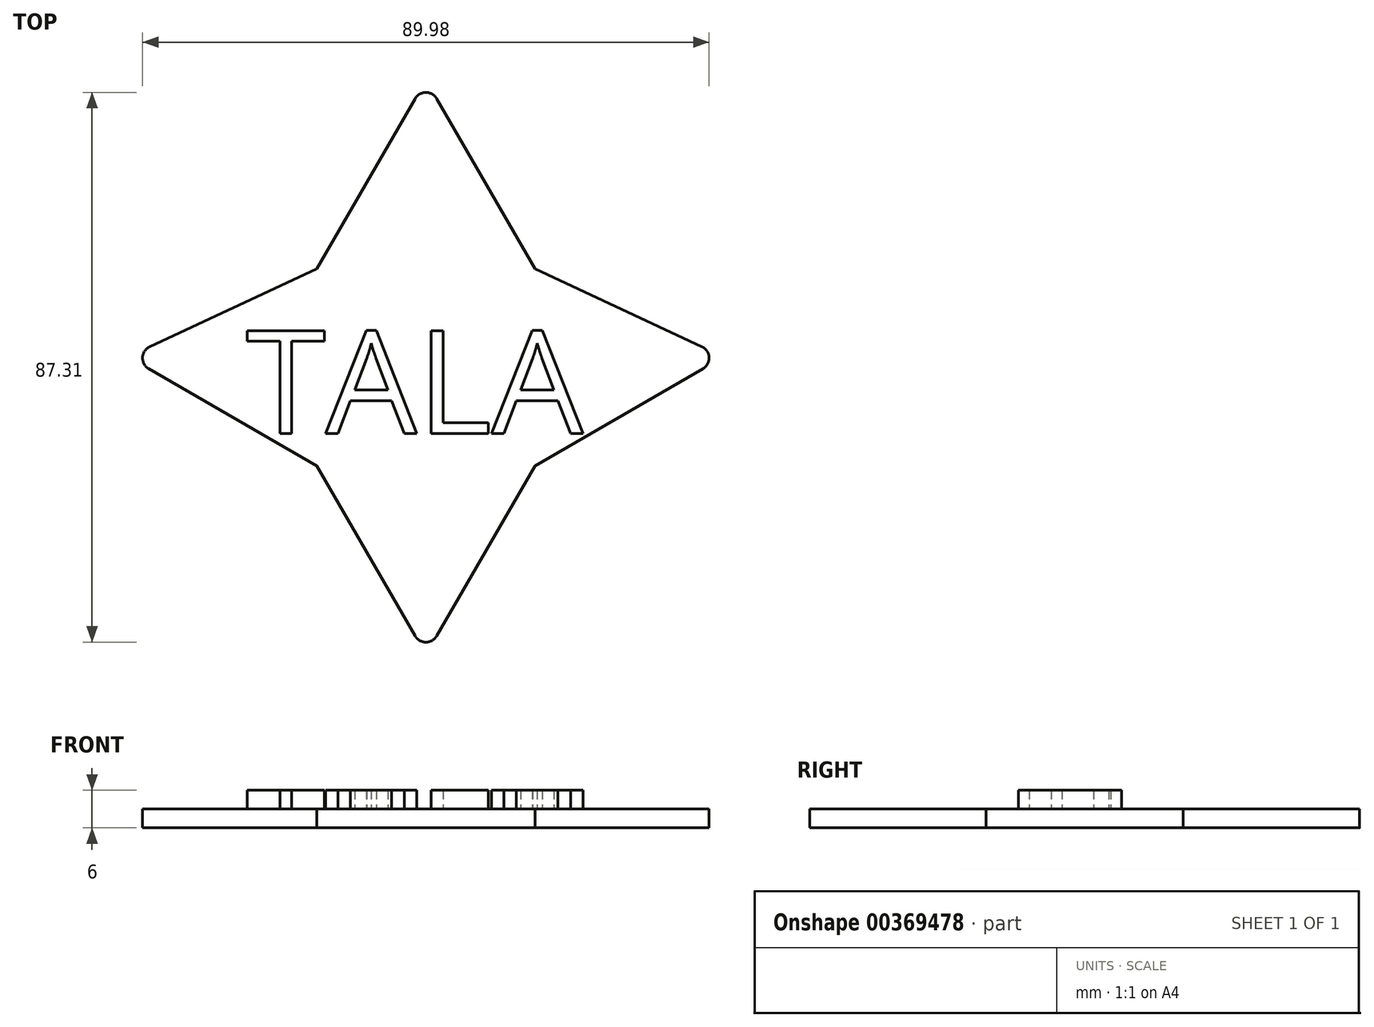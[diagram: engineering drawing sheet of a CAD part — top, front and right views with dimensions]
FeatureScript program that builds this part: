
annotation { "Feature Type Name" : "Feature", "Feature Type Description" : "" }
export const myFeature = defineFeature(function(context is Context, id is Id, definition is map)
    precondition{}
    {
        {
            var Q0;
            Q0=qCreatedBy(makeId("Top.planeOp"),FACE);
            var sketch = newSketch(context, id + "F0", { "sketchPlane" : qUnion([Q0])});
            skLineSegment(sketch, "E0", {"start": v(0, 0) * mm, "end": v(15.59, 27) * mm});
            skLineSegment(sketch, "E1", {"start": v(19.05, 27) * mm, "end": v(34.64, 0) * mm});
            skLineSegment(sketch, "E2", {"start": v(0, 0) * mm, "end": v(-26.52, -12.37) * mm});
            skLineSegment(sketch, "E3", {"start": v(-26.67, -15.91) * mm, "end": v(0, -31.3) * mm});
            skLineSegment(sketch, "E4", {"start": v(17.32, 30) * mm, "end": v(17.32, -23.52) * mm, "construction": true});
            skLineSegment(sketch, "E5.MirrorCS", {"start": v(34.64, 0) * mm, "end": v(61.16, -12.37) * mm});
            skLineSegment(sketch, "E6.MirrorCS", {"start": v(61.31, -15.91) * mm, "end": v(34.64, -31.3) * mm});
            skLineSegment(sketch, "E7", {"start": v(34.64, -31.3) * mm, "end": v(19.05, -58.3) * mm});
            skLineSegment(sketch, "E8", {"start": v(15.59, -58.3) * mm, "end": v(0, -31.3) * mm});
            skPoint(sketch, "E9.visualSharp", {"position": v(17.32, 30) * mm});
            skArc(sketch, "E9.filletArc", {"start": v(19.05, 27) * mm, "mid": v(17.32, 28) * mm, "end": v(15.59, 27) * mm});
            skPoint(sketch, "E10.visualSharp", {"position": v(64.64, -13.99) * mm});
            skArc(sketch, "E10.filletArc", {"start": v(61.31, -15.91) * mm, "mid": v(62.31, -14.1) * mm, "end": v(61.16, -12.37) * mm});
            skPoint(sketch, "E11.visualSharp", {"position": v(17.32, -61.3) * mm});
            skArc(sketch, "E11.filletArc", {"start": v(15.59, -58.3) * mm, "mid": v(17.32, -59.3) * mm, "end": v(19.05, -58.3) * mm});
            skPoint(sketch, "E12.visualSharp", {"position": v(-30, -13.99) * mm});
            skArc(sketch, "E12.filletArc", {"start": v(-26.52, -12.37) * mm, "mid": v(-27.67, -14.1) * mm, "end": v(-26.67, -15.91) * mm});
            skSolve(sketch);
        }
        {
            var Q0;
            Q0 = qSketchRegion(id + "F0", true);
            extrude(context, id + "F1", {"entities" : qUnion([Q0]), "depth" : 3 * mm});
        }
        {
            var Q0;
            Q0=makeQuery(id+"F1.opExtrude","CAP_FACE",FACE,{"disambiguationData":[OSD([sQuery(id+"F0.wireOp",EDGE,"E0"),sQuery(id+"F0.wireOp",EDGE,"E1"),sQuery(id+"F0.wireOp",EDGE,"E2"),sQuery(id+"F0.wireOp",EDGE,"E3"),sQuery(id+"F0.wireOp",EDGE,"E5.MirrorCS"),sQuery(id+"F0.wireOp",EDGE,"E6.MirrorCS"),sQuery(id+"F0.wireOp",EDGE,"E7"),sQuery(id+"F0.wireOp",EDGE,"E8")])],"isStart":false});
            var sketch = newSketch(context, id + "F2", { "sketchPlane" : qUnion([Q0])});
            skText(sketch, "E13", { "text": "TALA", "fontName": "OpenSans-Regular.ttf"});
            const initialGuessF2  = {"E13": [-0.01125, -0.02618, 1, 0, 0.01648]};
            skSetInitialGuess(sketch, initialGuessF2);
            skSolve(sketch);
        }
        {
            var Q0;
            Q0 = qSketchRegion(id + "F2", true);
            extrude(context, id + "F3", {"entities" : qUnion([Q0]), "operationType" : NewBodyOperationType.ADD, "depth" : 3 * mm});
        }
    });
